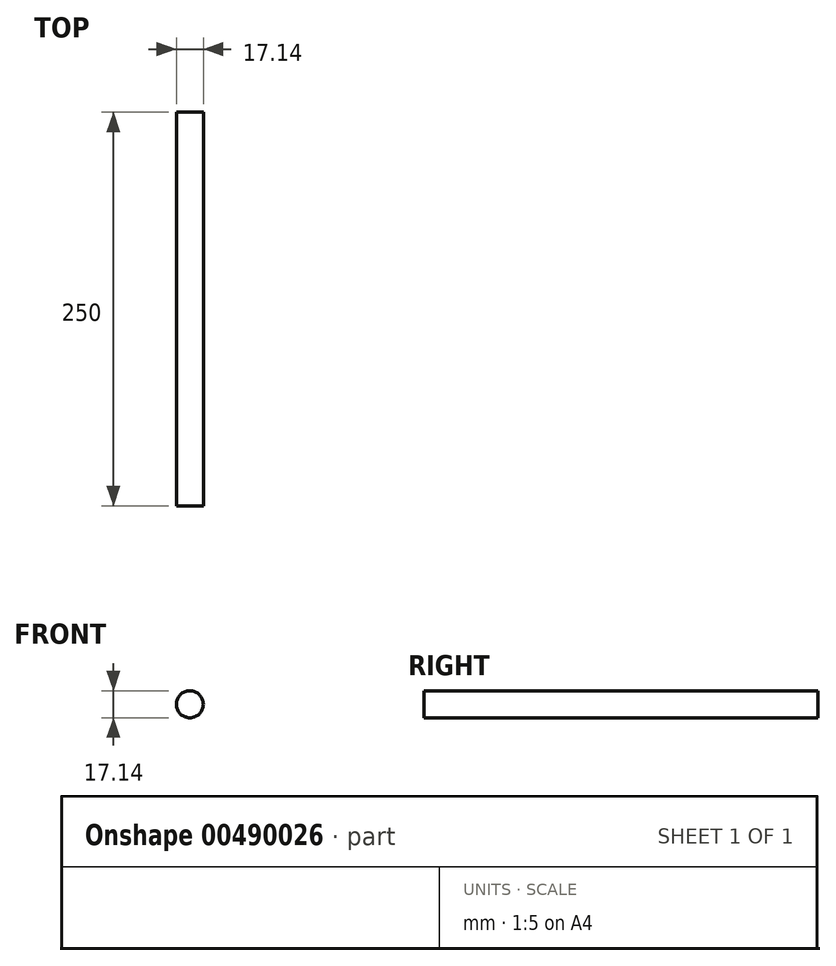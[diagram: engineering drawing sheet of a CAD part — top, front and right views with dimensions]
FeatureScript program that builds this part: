
annotation { "Feature Type Name" : "Feature", "Feature Type Description" : "" }
export const myFeature = defineFeature(function(context is Context, id is Id, definition is map)
    precondition{}
    {
        {
            var Q0;
            Q0=qCreatedBy(makeId("Front.planeOp"),FACE);
            var sketch = newSketch(context, id + "F0", { "sketchPlane" : qUnion([Q0])});
            skCircle(sketch, "E0", {"center": v(0, 0) * mm, "radius": 8.57 * mm});
            skSolve(sketch);
        }
        {
            var Q0;
            Q0=makeQuery(id+"F0.imprint","IMPRINT",FACE,{"disambiguationData":[TD([[makeQuery(id+"F0.imprint","IMPRINT",EDGE,{"derivedFrom":sQuery(id+"F0.wireOp",EDGE,"E0")}),1.0]])]});
            extrude(context, id + "F1", {"entities" : qUnion([Q0]), "depth" : 250 * mm});
        }
    });
